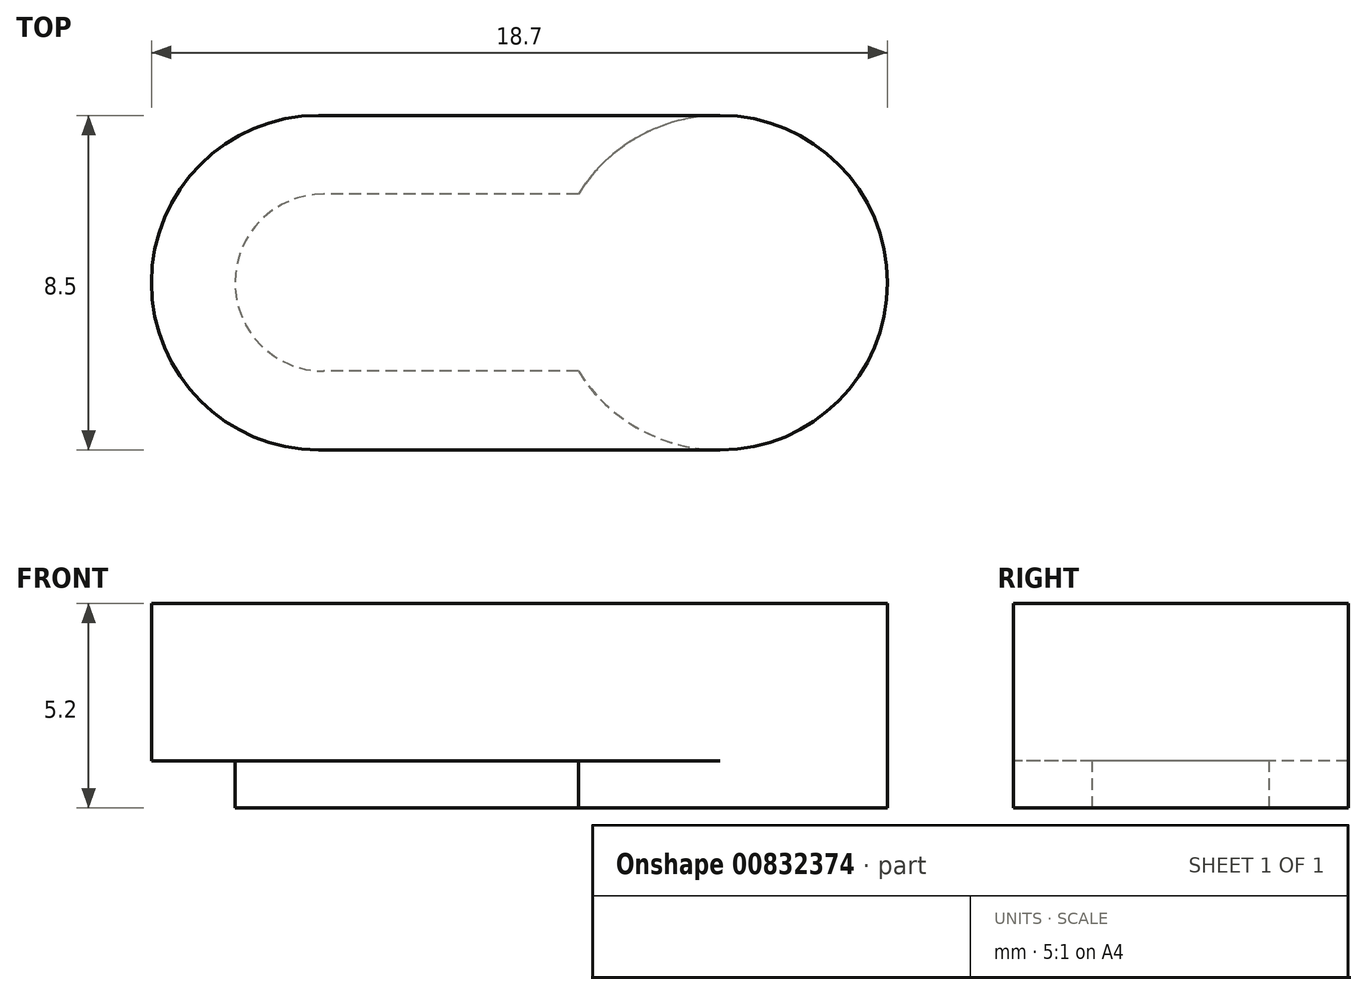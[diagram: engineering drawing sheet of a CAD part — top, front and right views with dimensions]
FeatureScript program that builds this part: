
annotation { "Feature Type Name" : "Feature", "Feature Type Description" : "" }
export const myFeature = defineFeature(function(context is Context, id is Id, definition is map)
    precondition{}
    {
        {
            assignVariable(context, id + "F0", {"name" : "ShaftWidth", "anyValue" : 4.5});
        }
        {
            assignVariable(context, id + "F1", {"name" : "WallGap", "anyValue" : .2});
        }
        {
            assignVariable(context, id + "F2", {"name" : "ScrewHeadHeight", "anyValue" : 4});
        }
        {
            assignVariable(context, id + "F3", {"name" : "BaseThickness", "anyValue" : 1.2});
        }
        {
            var Q0;
            Q0=qCreatedBy(makeId("Top.planeOp"),FACE);
            var sketch = newSketch(context, id + "F4", { "sketchPlane" : qUnion([Q0])});
            skCircle(sketch, "E0", {"center": v(8.35, 0) * mm, "radius": 4.25 * mm, "construction": true});
            skLineSegment(sketch, "E1.bottom", {"start": v(8.35, 2.25) * mm, "end": v(-3.98, 2.25) * mm, "construction": true});
            skLineSegment(sketch, "E1.top", {"start": v(8.35, -2.25) * mm, "end": v(-3.98, -2.25) * mm, "construction": true});
            skLineSegment(sketch, "E1.left", {"start": v(8.35, 2.25) * mm, "end": v(8.35, -2.25) * mm, "construction": true});
            skLineSegment(sketch, "E1.right", {"start": v(-3.98, 2.25) * mm, "end": v(-3.98, -2.25) * mm, "construction": true});
            skCircle(sketch, "E2", {"center": v(-1.85, 0) * mm, "radius": 4.25 * mm, "construction": true});
            skLineSegment(sketch, "E3.bottom", {"start": v(12.8, 4.45) * mm, "end": v(-6.3, 4.45) * mm, "construction": true});
            skLineSegment(sketch, "E3.top", {"start": v(12.8, -4.45) * mm, "end": v(-6.3, -4.45) * mm, "construction": true});
            skLineSegment(sketch, "E3.left", {"start": v(12.8, 4.45) * mm, "end": v(12.8, -4.45) * mm, "construction": true});
            skLineSegment(sketch, "E3.right", {"start": v(-6.3, 4.45) * mm, "end": v(-6.3, -4.45) * mm, "construction": true});
            skPoint(sketch, "E3.middle", {"position": v(3.25, 0) * mm});
            skPoint(sketch, "E3.middle.positionSnap0", {"position": v(3.25, -2.25) * mm});
            skPoint(sketch, "E3.centerSnap0", {"position": v(3.25, -2.25) * mm});
            skSolve(sketch);
        }
        {
            var Q0;
            Q0=qCreatedBy(makeId("Top.planeOp"),FACE);
            cPlane(context, id + "F5", {"entities" : qUnion([Q0]), "cplaneType" : CPlaneType.OFFSET, "offset" : (getVariable(context, 'BaseThickness')) * mm, "width" : 150 * mm, "height" : 150 * mm});
        }
        {
            var Q0;
            Q0=qCreatedBy(makeId("Top.planeOp"),FACE);
            var sketch = newSketch(context, id + "F6", { "sketchPlane" : qUnion([Q0])});
            skLineSegment(sketch, "E4.bottom", {"start": v(-6.3, -4.45) * mm, "end": v(12.8, -4.45) * mm});
            skLineSegment(sketch, "E4.top", {"start": v(-6.3, 4.45) * mm, "end": v(12.8, 4.45) * mm});
            skLineSegment(sketch, "E4.left", {"start": v(-6.3, -4.45) * mm, "end": v(-6.3, 4.45) * mm});
            skLineSegment(sketch, "E4.right", {"start": v(12.8, -4.45) * mm, "end": v(12.8, 4.45) * mm});
            skSolve(sketch);
        }
        {
            var Q0;
            Q0 = qSketchRegion(id + "F6", true);
            var Q1;
            Q1=qCreatedBy(id+"F5.planeOp",FACE);
            extrude(context, id + "F7", {"entities" : qUnion([Q0]), "endBound" : BoundingType.UP_TO_SURFACE, "depth" : (getVariable(context, 'BaseThickness') + getVariable(context, 'ScrewHeadHeight') + getVariable(context, 'WallGap')) * mm, "endBoundEntityFace" : qUnion([Q1]), "offsetDistance" : 25 * mm});
        }
        {
            var Q0;
            Q0=makeQuery(id+"F7.opExtrude","CAP_FACE",FACE,{"disambiguationData":[OSD([sQuery(id+"F6.wireOp",EDGE,"E4.bottom"),sQuery(id+"F6.wireOp",EDGE,"E4.top"),sQuery(id+"F6.wireOp",EDGE,"E4.left"),sQuery(id+"F6.wireOp",EDGE,"E4.right")])],"isStart":false});
            var sketch = newSketch(context, id + "F8", { "sketchPlane" : qUnion([Q0])});
            skLineSegment(sketch, "E5.bottom", {"start": v(-3.98, 2.25) * mm, "end": v(4.74, 2.25) * mm});
            skLineSegment(sketch, "E5.top", {"start": v(-3.98, -2.25) * mm, "end": v(4.74, -2.25) * mm});
            skLineSegment(sketch, "E5.left", {"start": v(-3.98, 2.25) * mm, "end": v(-3.98, -2.25) * mm});
            skPoint(sketch, "E6.orphan", {"position": v(8.35, 2.25) * mm});
            skPoint(sketch, "E7.orphan", {"position": v(8.47, -2.25) * mm});
            skCircle(sketch, "E8", {"center": v(8.35, 0) * mm, "radius": 4.25 * mm});
            skSolve(sketch);
        }
        {
            var Q0;
            Q0=qCreatedBy(id+"F5.planeOp",FACE);
            var sketch = newSketch(context, id + "F9", { "sketchPlane" : qUnion([Q0])});
            skArc(sketch, "E9", {"start": v(8.35, -4.25) * mm, "mid": v(12.6, 0) * mm, "end": v(8.35, 4.25) * mm});
            skLineSegment(sketch, "E10.bottom", {"start": v(-1.85, 4.25) * mm, "end": v(8.35, 4.25) * mm});
            skLineSegment(sketch, "E10.top", {"start": v(-1.85, -4.25) * mm, "end": v(8.35, -4.25) * mm});
            skLineSegment(sketch, "E10.left", {"start": v(-1.85, 4.25) * mm, "end": v(-1.85, -4.25) * mm, "construction": true});
            skLineSegment(sketch, "E10.right", {"start": v(8.35, 4.25) * mm, "end": v(8.35, -4.25) * mm, "construction": true});
            skCircle(sketch, "E11", {"center": v(-1.85, 0) * mm, "radius": 4.25 * mm});
            skSolve(sketch);
        }
        {
            var Q0;
            Q0 = qSketchRegion(id + "F8", true);
            var Q1;
            Q1=makeQuery(id+"F7.opExtrude","CAP_FACE",FACE,{"disambiguationData":[OSD([sQuery(id+"F6.wireOp",EDGE,"E4.bottom"),sQuery(id+"F6.wireOp",EDGE,"E4.top"),sQuery(id+"F6.wireOp",EDGE,"E4.left"),sQuery(id+"F6.wireOp",EDGE,"E4.right")])],"isStart":true});
            extrude(context, id + "F10", {"entities" : qUnion([Q0]), "operationType" : NewBodyOperationType.REMOVE, "endBound" : BoundingType.UP_TO_SURFACE, "oppositeDirection" : true, "depth" : 25 * mm, "endBoundEntityFace" : qUnion([Q1]), "offsetDistance" : 25 * mm});
        }
        {
            var Q0;
            Q0=makeQuery(id+"F10.boolean.opBoolean","COPY",EDGE,{"derivedFrom":makeQuery(id+"F10.opExtrude","SWEPT_EDGE",EDGE,{"disambiguationData":[OSD([sQuery(id+"F8.wireOp",EDGE,"E5.bottom"),sQuery(id+"F8.wireOp",EDGE,"E5.left")])]})});
            var Q1;
            Q1=makeQuery(id+"F10.boolean.opBoolean","COPY",EDGE,{"derivedFrom":makeQuery(id+"F10.opExtrude","SWEPT_EDGE",EDGE,{"disambiguationData":[OSD([sQuery(id+"F8.wireOp",EDGE,"E5.top"),sQuery(id+"F8.wireOp",EDGE,"E5.left")])]})});
            fillet(context, id + "F11", {"entities" : qUnion([Q0, Q1]), "radius" : (getVariable(context, 'ShaftWidth') / 2) * mm, "tangentPropagation" : true, "allowEdgeOverflow" : false});
        }
        {
            var Q0;
            Q0=makeQuery(id+"F7.opExtrude","CAP_FACE",FACE,{"disambiguationData":[OSD([sQuery(id+"F6.wireOp",EDGE,"E4.bottom"),sQuery(id+"F6.wireOp",EDGE,"E4.top"),sQuery(id+"F6.wireOp",EDGE,"E4.left"),sQuery(id+"F6.wireOp",EDGE,"E4.right")])],"isStart":false});
            var sketch = newSketch(context, id + "F12", { "sketchPlane" : qUnion([Q0])});
            skLineSegment(sketch, "E12.bottom", {"start": v(-6.3, 4.45) * mm, "end": v(12.8, 4.45) * mm});
            skLineSegment(sketch, "E12.top", {"start": v(-6.3, -4.45) * mm, "end": v(12.8, -4.45) * mm});
            skLineSegment(sketch, "E12.left", {"start": v(-6.3, 4.45) * mm, "end": v(-6.3, -4.45) * mm});
            skLineSegment(sketch, "E12.right", {"start": v(12.8, 4.45) * mm, "end": v(12.8, -4.45) * mm});
            skSolve(sketch);
        }
        {
            var Q0;
            Q0 = qSketchRegion(id + "F12", true);
            extrude(context, id + "F13", {"entities" : qUnion([Q0]), "operationType" : NewBodyOperationType.ADD, "depth" : (getVariable(context, 'ScrewHeadHeight') + getVariable(context, 'WallGap')) * mm, "offsetDistance" : 25 * mm});
        }
        {
            var Q0;
            Q0 = qSketchRegion(id + "F9", true);
            var Q1;
            Q1=makeQuery(id+"F13.opExtrude","CAP_FACE",FACE,{"disambiguationData":[OSD([sQuery(id+"F12.wireOp",EDGE,"E12.bottom"),sQuery(id+"F12.wireOp",EDGE,"E12.top"),sQuery(id+"F12.wireOp",EDGE,"E12.left"),sQuery(id+"F12.wireOp",EDGE,"E12.right")])],"isStart":false});
            extrude(context, id + "F14", {"entities" : qUnion([Q0]), "operationType" : NewBodyOperationType.REMOVE, "endBound" : BoundingType.UP_TO_SURFACE, "depth" : 25 * mm, "endBoundEntityFace" : qUnion([Q1]), "hasOffset" : true, "offsetDistance" : (getVariable(context, 'WallGap')) * mm});
        }
        {
            var Q0;
            Q0=makeQuery(id+"F7.opExtrude","CAP_FACE",FACE,{"disambiguationData":[OSD([sQuery(id+"F6.wireOp",EDGE,"E4.bottom"),sQuery(id+"F6.wireOp",EDGE,"E4.top"),sQuery(id+"F6.wireOp",EDGE,"E4.left"),sQuery(id+"F6.wireOp",EDGE,"E4.right")])],"isStart":true});
            var sketch = newSketch(context, id + "F15", { "sketchPlane" : qUnion([Q0])});
            skLineSegment(sketch, "E13.bottom", {"start": v(-6.3, -4.45) * mm, "end": v(12.8, -4.45) * mm});
            skLineSegment(sketch, "E13.top", {"start": v(-6.3, 4.45) * mm, "end": v(12.8, 4.45) * mm});
            skLineSegment(sketch, "E13.left", {"start": v(-6.3, -4.45) * mm, "end": v(-6.3, 4.45) * mm});
            skLineSegment(sketch, "E13.right", {"start": v(12.8, -4.45) * mm, "end": v(12.8, 4.45) * mm});
            skSolve(sketch);
        }
        {
            var Q0;
            Q0 = qSketchRegion(id + "F15", true);
            var Q1;
            Q1=makeQuery(id+"F7.opExtrude","SWEPT_BODY",BODY,{"disambiguationData":[OSD([sQuery(id+"F6.wireOp",EDGE,"E4.bottom"),sQuery(id+"F6.wireOp",EDGE,"E4.top"),sQuery(id+"F6.wireOp",EDGE,"E4.left"),sQuery(id+"F6.wireOp",EDGE,"E4.right")])]});
            extrude(context, id + "F16", {"entities" : qUnion([Q0]), "endBound" : BoundingType.UP_TO_BODY, "oppositeDirection" : true, "depth" : 25 * mm, "endBoundEntityBody" : qUnion([Q1]), "offsetDistance" : 25 * mm});
        }
        {
            var Q0;
            Q0=makeQuery(id+"F7.opExtrude","SWEPT_BODY",BODY,{"disambiguationData":[OSD([sQuery(id+"F6.wireOp",EDGE,"E4.bottom"),sQuery(id+"F6.wireOp",EDGE,"E4.top"),sQuery(id+"F6.wireOp",EDGE,"E4.left"),sQuery(id+"F6.wireOp",EDGE,"E4.right")])]});
            var Q1;
            Q1=makeQuery(id+"F16.opExtrude","SWEPT_BODY",BODY,{"disambiguationData":[OSD([sQuery(id+"F15.wireOp",EDGE,"E13.bottom"),sQuery(id+"F15.wireOp",EDGE,"E13.top"),sQuery(id+"F15.wireOp",EDGE,"E13.left"),sQuery(id+"F15.wireOp",EDGE,"E13.right")])]});
            booleanBodies(context, id + "F17", {"operationType" : BooleanOperationType.SUBTRACTION, "tools" : qUnion([Q0]), "targets" : qUnion([Q1])});
        }
    });
